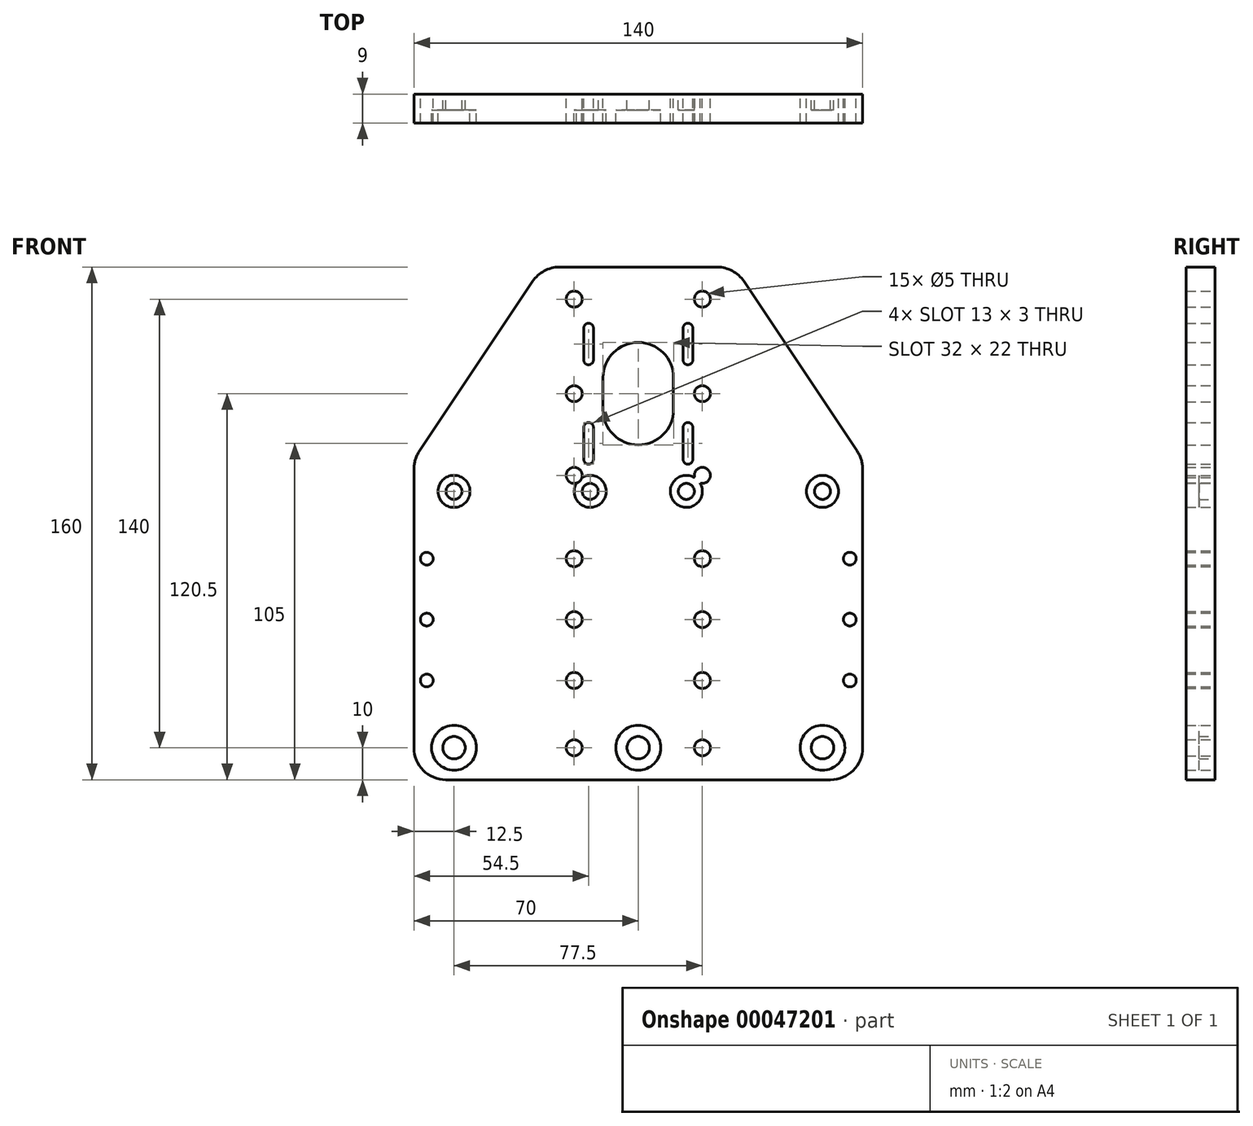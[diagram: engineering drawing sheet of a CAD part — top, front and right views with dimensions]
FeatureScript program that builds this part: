
annotation { "Feature Type Name" : "Feature", "Feature Type Description" : "" }
export const myFeature = defineFeature(function(context is Context, id is Id, definition is map)
    precondition{}
    {
        {
            var Q0;
            Q0=qCreatedBy(makeId("Front.planeOp"),FACE);
            var sketch = newSketch(context, id + "F0", { "sketchPlane" : qUnion([Q0])});
            skLineSegment(sketch, "E0.bottom", {"start": v(-60, 0) * mm, "end": v(60, 0) * mm});
            skLineSegment(sketch, "E0.top", {"start": v(-24.65, 160) * mm, "end": v(30, 160) * mm});
            skLineSegment(sketch, "E0.left", {"start": v(-70, 10) * mm, "end": v(-70, 96.97) * mm});
            skLineSegment(sketch, "E0.right", {"start": v(70, 10) * mm, "end": v(70, 100) * mm});
            skCircle(sketch, "E1", {"center": v(-57.5, 10) * mm, "radius": 3.5 * mm});
            skCircle(sketch, "E2", {"center": v(-57.5, 90) * mm, "radius": 2.5 * mm});
            skCircle(sketch, "E3.MirrorC", {"center": v(57.5, 10) * mm, "radius": 3.5 * mm});
            skCircle(sketch, "E4.MirrorC", {"center": v(57.5, 90) * mm, "radius": 2.5 * mm});
            skCircle(sketch, "E5", {"center": v(-20, 10) * mm, "radius": 2.5 * mm});
            skCircle(sketch, "E6.MirrorC", {"center": v(20, 10) * mm, "radius": 2.5 * mm});
            skCircle(sketch, "E7", {"center": v(-20, 150) * mm, "radius": 2.5 * mm});
            skCircle(sketch, "E8.MirrorC", {"center": v(20, 150) * mm, "radius": 2.5 * mm});
            skLineSegment(sketch, "E9", {"start": v(-15.5, 110) * mm, "end": v(-15.5, 100) * mm, "construction": true});
            skArc(sketch, "E10", {"start": v(11, 125.5) * mm, "mid": v(0, 136.5) * mm, "end": v(-11, 125.5) * mm});
            skLineSegment(sketch, "E11.MirrorCS", {"start": v(-14, 141) * mm, "end": v(-14, 131) * mm});
            skArc(sketch, "E12", {"start": v(-11, 115.5) * mm, "mid": v(0, 104.5) * mm, "end": v(11, 115.5) * mm});
            skLineSegment(sketch, "E13", {"start": v(-11, 125.5) * mm, "end": v(-11, 115.5) * mm});
            skLineSegment(sketch, "E14", {"start": v(11, 125.5) * mm, "end": v(11, 115.5) * mm});
            skLineSegment(sketch, "E15", {"start": v(-17, 141) * mm, "end": v(-17, 131) * mm});
            skLineSegment(sketch, "E16.MirrorCS", {"start": v(-14, 110) * mm, "end": v(-14, 100) * mm});
            skLineSegment(sketch, "E17", {"start": v(-17, 110) * mm, "end": v(-17, 100) * mm});
            skLineSegment(sketch, "E18", {"start": v(-15.5, 141) * mm, "end": v(-15.5, 131) * mm, "construction": true});
            skArc(sketch, "E19", {"start": v(-17, 131) * mm, "mid": v(-15.5, 129.5) * mm, "end": v(-14, 131) * mm});
            skArc(sketch, "E20", {"start": v(-14, 141) * mm, "mid": v(-15.5, 142.5) * mm, "end": v(-17, 141) * mm});
            skArc(sketch, "E21", {"start": v(-17, 100) * mm, "mid": v(-15.5, 98.5) * mm, "end": v(-14, 100) * mm});
            skArc(sketch, "E22.MirrorCS", {"start": v(-17, 110) * mm, "mid": v(-15.5, 111.5) * mm, "end": v(-14, 110) * mm});
            skArc(sketch, "E23.MirrorCS", {"start": v(-14, 100) * mm, "mid": v(-15.5, 98.5) * mm, "end": v(-17, 100) * mm});
            skArc(sketch, "E24", {"start": v(-14, 110) * mm, "mid": v(-15.5, 111.5) * mm, "end": v(-17, 110) * mm});
            skLineSegment(sketch, "E25", {"start": v(0, 125.5) * mm, "end": v(0, 115.5) * mm, "construction": true});
            skLineSegment(sketch, "E26.MirrorCS", {"start": v(17, 141) * mm, "end": v(17, 131) * mm});
            skLineSegment(sketch, "E27.MirrorCS", {"start": v(14, 141) * mm, "end": v(14, 131) * mm});
            skArc(sketch, "E28.MirrorCS", {"start": v(14, 141) * mm, "mid": v(15.5, 142.5) * mm, "end": v(17, 141) * mm});
            skArc(sketch, "E29.MirrorCS", {"start": v(17, 131) * mm, "mid": v(15.5, 129.5) * mm, "end": v(14, 131) * mm});
            skLineSegment(sketch, "E30.MirrorCS", {"start": v(15.5, 141) * mm, "end": v(15.5, 131) * mm, "construction": true});
            skLineSegment(sketch, "E31.MirrorCS", {"start": v(17, 110) * mm, "end": v(17, 100) * mm});
            skArc(sketch, "E32.MirrorCS", {"start": v(17, 110) * mm, "mid": v(15.5, 111.5) * mm, "end": v(14, 110) * mm});
            skLineSegment(sketch, "E33.MirrorCS", {"start": v(14, 110) * mm, "end": v(14, 100) * mm});
            skArc(sketch, "E34.MirrorCS", {"start": v(17, 100) * mm, "mid": v(15.5, 98.5) * mm, "end": v(14, 100) * mm});
            skArc(sketch, "E35.MirrorCS", {"start": v(14, 110) * mm, "mid": v(15.5, 111.5) * mm, "end": v(17, 110) * mm});
            skLineSegment(sketch, "E36.MirrorCS", {"start": v(15.5, 110) * mm, "end": v(15.5, 100) * mm, "construction": true});
            skArc(sketch, "E37.MirrorCS", {"start": v(14, 100) * mm, "mid": v(15.5, 98.5) * mm, "end": v(17, 100) * mm});
            skCircle(sketch, "E38", {"center": v(-15, 90) * mm, "radius": 2.5 * mm});
            skCircle(sketch, "E39.MirrorC", {"center": v(15, 90) * mm, "radius": 2.5 * mm});
            skPoint(sketch, "E40.visualSharp", {"position": v(-70, 0) * mm});
            skArc(sketch, "E40.filletArc", {"start": v(-70, 10) * mm, "mid": v(-67.07, 2.93) * mm, "end": v(-60, 0) * mm});
            skLineSegment(sketch, "E41", {"start": v(-32.97, 155.55) * mm, "end": v(-68.32, 102.52) * mm});
            skPoint(sketch, "E42.newPointB", {"position": v(-30, 160) * mm});
            skArc(sketch, "E42.filletArc", {"start": v(-24.65, 160) * mm, "mid": v(-29.37, 158.82) * mm, "end": v(-32.97, 155.55) * mm});
            skPoint(sketch, "E43.newPointA", {"position": v(-70, 100) * mm});
            skArc(sketch, "E43.filletArc", {"start": v(-68.32, 102.52) * mm, "mid": v(-69.57, 99.87) * mm, "end": v(-70, 96.97) * mm});
            skPoint(sketch, "E44.visualSharp", {"position": v(70, 0) * mm});
            skArc(sketch, "E44.filletArc", {"start": v(60, 0) * mm, "mid": v(67.07, 2.93) * mm, "end": v(70, 10) * mm});
            skLineSegment(sketch, "E45.MirrorCS", {"start": v(32.97, 155.55) * mm, "end": v(68.32, 102.52) * mm});
            skPoint(sketch, "E46.MirrorP", {"position": v(70, 100) * mm});
            skArc(sketch, "E47.MirrorCS", {"start": v(24.65, 160) * mm, "mid": v(29.37, 158.82) * mm, "end": v(32.97, 155.55) * mm});
            skArc(sketch, "E48.MirrorCS", {"start": v(68.32, 102.52) * mm, "mid": v(69.57, 99.87) * mm, "end": v(70, 96.97) * mm});
            skPoint(sketch, "E49.MirrorP", {"position": v(30, 160) * mm});
            skCircle(sketch, "E50", {"center": v(0, 10) * mm, "radius": 3.5 * mm});
            skCircle(sketch, "E51", {"center": v(-66, 50) * mm, "radius": 2 * mm});
            skCircle(sketch, "E52", {"center": v(-66, 31) * mm, "radius": 2 * mm});
            skCircle(sketch, "E53.MirrorC", {"center": v(66, 31) * mm, "radius": 2 * mm});
            skCircle(sketch, "E54.MirrorC", {"center": v(66, 50) * mm, "radius": 2 * mm});
            skCircle(sketch, "E55", {"center": v(-66, 69) * mm, "radius": 2 * mm});
            skCircle(sketch, "E56.MirrorC", {"center": v(66, 69) * mm, "radius": 2 * mm});
            skCircle(sketch, "E57", {"center": v(-20, 50) * mm, "radius": 2.5 * mm});
            skCircle(sketch, "E58", {"center": v(-20, 69) * mm, "radius": 2.5 * mm});
            skCircle(sketch, "E59", {"center": v(-20, 120.5) * mm, "radius": 2.5 * mm});
            skCircle(sketch, "E60", {"center": v(-20, 31) * mm, "radius": 2.5 * mm});
            skCircle(sketch, "E61", {"center": v(-20, 95) * mm, "radius": 2.5 * mm});
            skCircle(sketch, "E62.MirrorC", {"center": v(20, 69) * mm, "radius": 2.5 * mm});
            skCircle(sketch, "E63.MirrorC", {"center": v(20, 50) * mm, "radius": 2.5 * mm});
            skCircle(sketch, "E64.MirrorC", {"center": v(20, 31) * mm, "radius": 2.5 * mm});
            skCircle(sketch, "E65.MirrorC", {"center": v(20, 95) * mm, "radius": 2.5 * mm});
            skCircle(sketch, "E66.MirrorC", {"center": v(20, 120.5) * mm, "radius": 2.5 * mm});
            skCircle(sketch, "E67", {"center": v(-57.5, 90) * mm, "radius": 5 * mm});
            skCircle(sketch, "E68", {"center": v(-57.5, 10) * mm, "radius": 7 * mm});
            skCircle(sketch, "E69", {"center": v(0, 10) * mm, "radius": 7 * mm});
            skCircle(sketch, "E70", {"center": v(-15, 90) * mm, "radius": 5 * mm});
            skCircle(sketch, "E71.MirrorC", {"center": v(15, 90) * mm, "radius": 5 * mm});
            skCircle(sketch, "E72.MirrorC", {"center": v(57.5, 90) * mm, "radius": 5 * mm});
            skCircle(sketch, "E73.MirrorC", {"center": v(57.5, 10) * mm, "radius": 7 * mm});
            skSolve(sketch);
        }
        {
            var Q0;
            Q0=makeQuery(id+"F0.imprint","IMPRINT",FACE,{"disambiguationData":[TD([[makeQuery(id+"F0.imprint","IMPRINT",EDGE,{"derivedFrom":sQuery(id+"F0.wireOp",EDGE,"E0.bottom")}),1.0]])]});
            extrude(context, id + "F1", {"entities" : qUnion([Q0]), "depth" : 9 * mm});
        }
        {
            var Q0;
            Q0=makeQuery(id+"F0.imprint","IMPRINT",FACE,{"disambiguationData":[TD([[makeQuery(id+"F0.imprint","IMPRINT",EDGE,{"derivedFrom":sQuery(id+"F0.wireOp",EDGE,"E2")}),-1.0]])]});
            var Q1;
            Q1=makeQuery(id+"F0.imprint","IMPRINT",FACE,{"disambiguationData":[TD([[makeQuery(id+"F0.imprint","IMPRINT",EDGE,{"derivedFrom":sQuery(id+"F0.wireOp",EDGE,"E38")}),-1.0]])]});
            var Q2;
            Q2=makeQuery(id+"F0.imprint","IMPRINT",FACE,{"disambiguationData":[TD([[makeQuery(id+"F0.imprint","IMPRINT",EDGE,{"derivedFrom":sQuery(id+"F0.wireOp",EDGE,"E39.MirrorC")}),1.0]])]});
            var Q3;
            Q3=makeQuery(id+"F0.imprint","IMPRINT",FACE,{"disambiguationData":[TD([[makeQuery(id+"F0.imprint","IMPRINT",EDGE,{"derivedFrom":sQuery(id+"F0.wireOp",EDGE,"E4.MirrorC")}),1.0]])]});
            var Q4;
            Q4=makeQuery(id+"F0.imprint","IMPRINT",FACE,{"disambiguationData":[TD([[makeQuery(id+"F0.imprint","IMPRINT",EDGE,{"derivedFrom":sQuery(id+"F0.wireOp",EDGE,"E3.MirrorC")}),1.0]])]});
            var Q5;
            Q5=makeQuery(id+"F0.imprint","IMPRINT",FACE,{"disambiguationData":[TD([[makeQuery(id+"F0.imprint","IMPRINT",EDGE,{"derivedFrom":sQuery(id+"F0.wireOp",EDGE,"E50")}),-1.0]])]});
            var Q6;
            Q6=makeQuery(id+"F0.imprint","IMPRINT",FACE,{"disambiguationData":[TD([[makeQuery(id+"F0.imprint","IMPRINT",EDGE,{"derivedFrom":sQuery(id+"F0.wireOp",EDGE,"E1")}),-1.0]])]});
            extrude(context, id + "F2", {"entities" : qUnion([Q0, Q1, Q2, Q3, Q4, Q5, Q6]), "operationType" : NewBodyOperationType.ADD, "depth" : 5 * mm});
        }
    });
